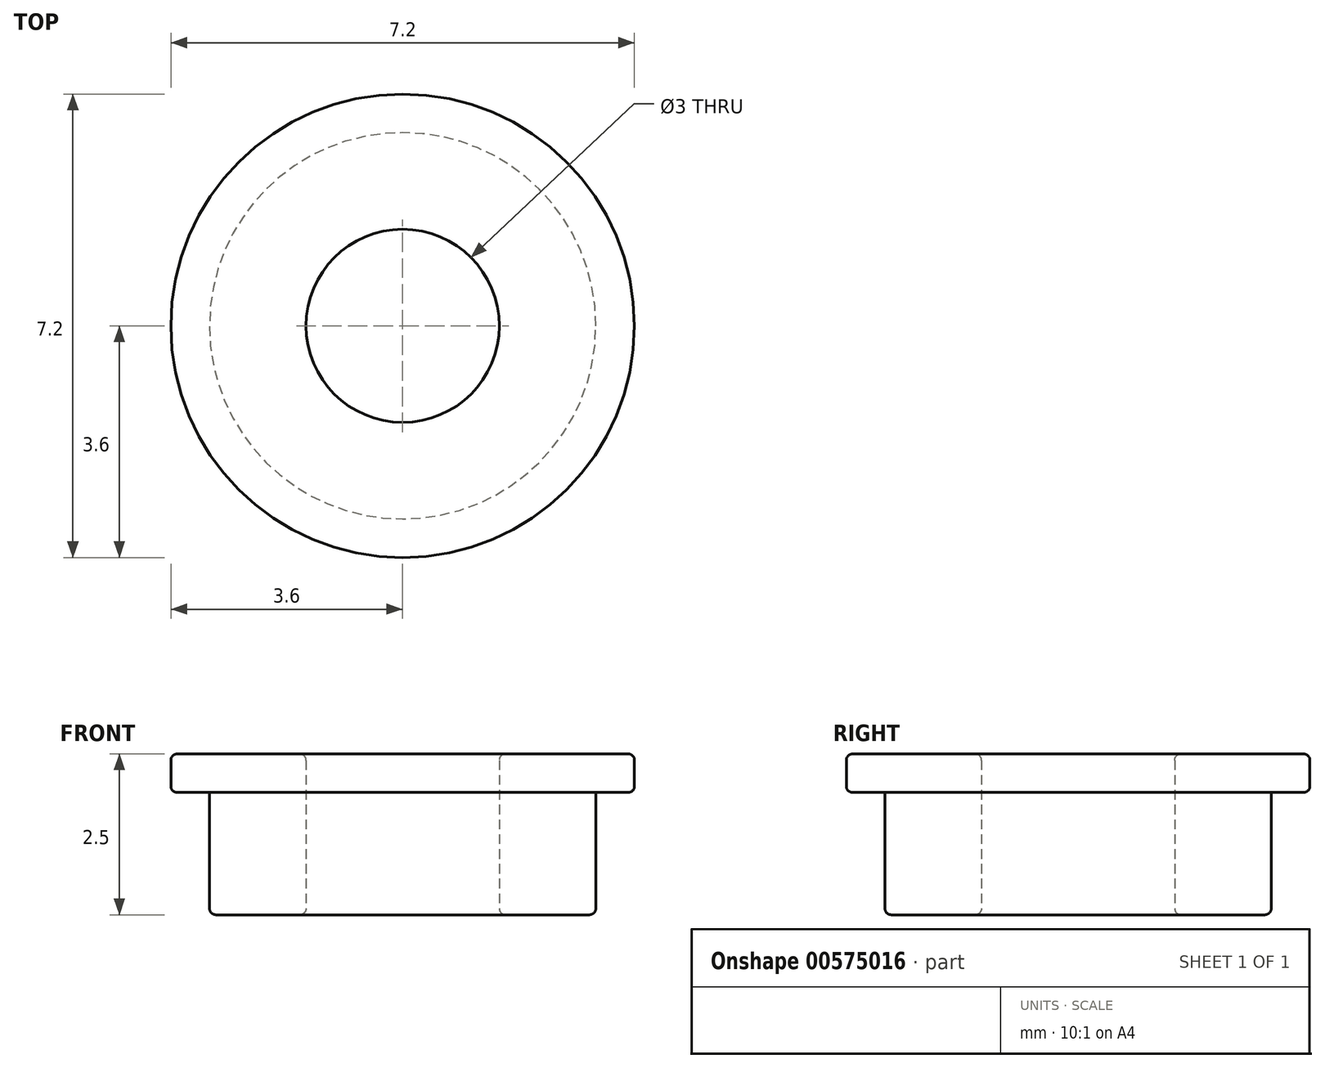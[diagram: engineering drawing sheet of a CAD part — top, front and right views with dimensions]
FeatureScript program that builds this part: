
annotation { "Feature Type Name" : "Feature", "Feature Type Description" : "" }
export const myFeature = defineFeature(function(context is Context, id is Id, definition is map)
    precondition{}
    {
        {
            var Q0;
            Q0=qCreatedBy(makeId("Top.planeOp"),FACE);
            var sketch = newSketch(context, id + "F0", { "sketchPlane" : qUnion([Q0])});
            skCircle(sketch, "E0", {"center": v(0, 0) * mm, "radius": 3 * mm});
            skCircle(sketch, "E1", {"center": v(0, 0) * mm, "radius": 1.5 * mm});
            skCircle(sketch, "E2", {"center": v(0, 0) * mm, "radius": 3.6 * mm});
            skSolve(sketch);
        }
        {
            var Q0;
            Q0 = qSketchRegion(id + "F0", true);
            var Q1;
            Q1=makeQuery(id+"F0.imprint","IMPRINT",FACE,{"disambiguationData":[TD([[makeQuery(id+"F0.imprint","IMPRINT",EDGE,{"derivedFrom":sQuery(id+"F0.wireOp",EDGE,"E0")}),1.0]])]});
            extrude(context, id + "F1", {"entities" : qUnion([Q0, Q1]), "depth" : 0.6 * mm, "offsetDistance" : 25 * mm});
        }
        {
            var Q0;
            Q0=makeQuery(id+"F0.imprint","IMPRINT",FACE,{"disambiguationData":[TD([[makeQuery(id+"F0.imprint","IMPRINT",EDGE,{"derivedFrom":sQuery(id+"F0.wireOp",EDGE,"E0")}),1.0]])]});
            extrude(context, id + "F2", {"entities" : qUnion([Q0]), "operationType" : NewBodyOperationType.ADD, "oppositeDirection" : true, "depth" : (2.5 - 0.6) * mm, "offsetDistance" : 25 * mm});
        }
        {
            var Q0;
            Q0=makeQuery(id+"F2.opExtrude","CAP_EDGE",EDGE,{"disambiguationData":[OSD([sQuery(id+"F0.wireOp",EDGE,"E0")])],"isStart":false});
            var Q1;
            Q1=makeQuery(id+"F2.opExtrude","CAP_EDGE",EDGE,{"disambiguationData":[OSD([sQuery(id+"F0.wireOp",EDGE,"E1")])],"isStart":false});
            var Q2;
            Q2=makeQuery(id+"F2.opExtrude","CAP_EDGE",EDGE,{"disambiguationData":[OSD([sQuery(id+"F0.wireOp",EDGE,"E0")])],"isStart":true});
            var Q3;
            Q3=makeQuery(id+"F1.opExtrude","CAP_EDGE",EDGE,{"disambiguationData":[OSD([sQuery(id+"F0.wireOp",EDGE,"E2")])],"isStart":true});
            var Q4;
            Q4=makeQuery(id+"F1.opExtrude","CAP_EDGE",EDGE,{"disambiguationData":[OSD([sQuery(id+"F0.wireOp",EDGE,"E2")])],"isStart":false});
            var Q5;
            Q5=makeQuery(id+"F1.opExtrude","CAP_EDGE",EDGE,{"disambiguationData":[OSD([sQuery(id+"F0.wireOp",EDGE,"E1")])],"isStart":false});
            fillet(context, id + "F3", {"entities" : qUnion([Q0, Q1, Q2, Q3, Q4, Q5]), "radius" : 0.1 * mm, "tangentPropagation" : true, "allowEdgeOverflow" : false});
        }
    });
